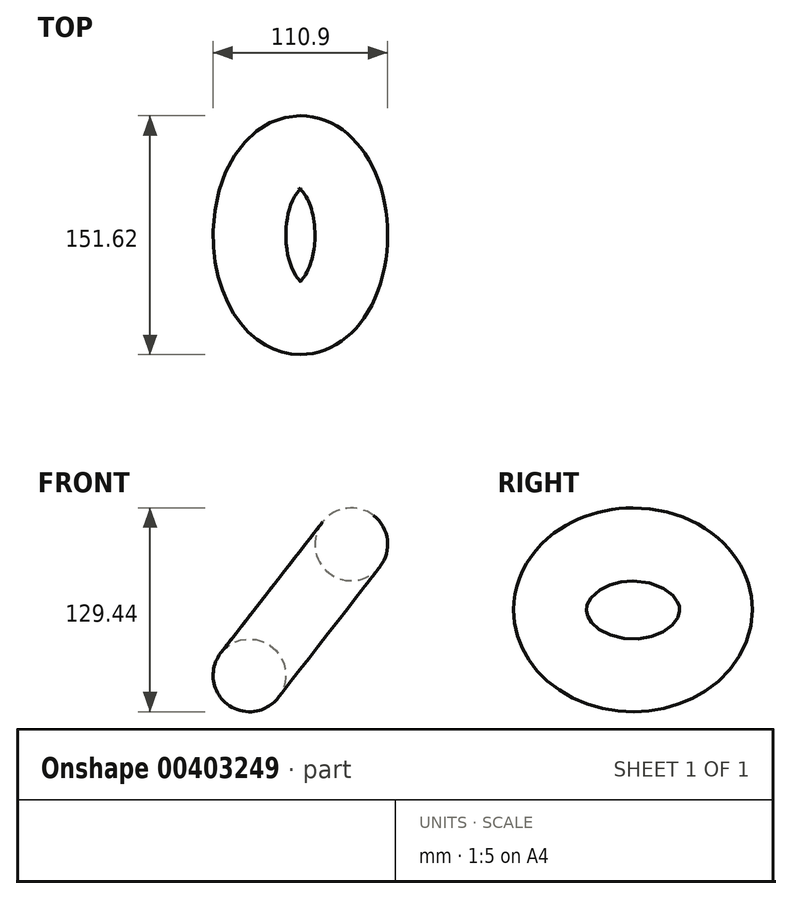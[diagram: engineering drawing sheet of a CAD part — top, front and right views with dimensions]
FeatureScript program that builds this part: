
annotation { "Feature Type Name" : "Feature", "Feature Type Description" : "" }
export const myFeature = defineFeature(function(context is Context, id is Id, definition is map)
    precondition{}
    {
        {
            var Q0;
            Q0=qCreatedBy(makeId("Front.planeOp"),FACE);
            var sketch = newSketch(context, id + "F0", { "sketchPlane" : qUnion([Q0])});
            skLineSegment(sketch, "E0", {"start": v(26.25, 37) * mm, "end": v(-47.27, 27.38) * mm});
            skLineSegment(sketch, "E1", {"start": v(-47.27, 27.38) * mm, "end": v(27.26, -30.55) * mm});
            skCircle(sketch, "E2", {"center": v(26.25, 37) * mm, "radius": 23.1 * mm});
            skSolve(sketch);
        }
        {
            var Q0;
            Q0=makeQuery(id+"F0.imprint","IMPRINT",FACE,{"disambiguationData":[TD([[makeQuery(id+"F0.imprint","IMPRINT",EDGE,{"derivedFrom":sQuery(id+"F0.wireOp",EDGE,"E2")}),1.0]])]});
            var Q1;
            Q1=sQuery(id+"F0.wireOp",EDGE,"E1");
            revolve(context, id + "F1", {"entities" : qUnion([Q0]), "axis" : qUnion([Q1]), "revolveType" : RevolveType.FULL});
        }
    });
